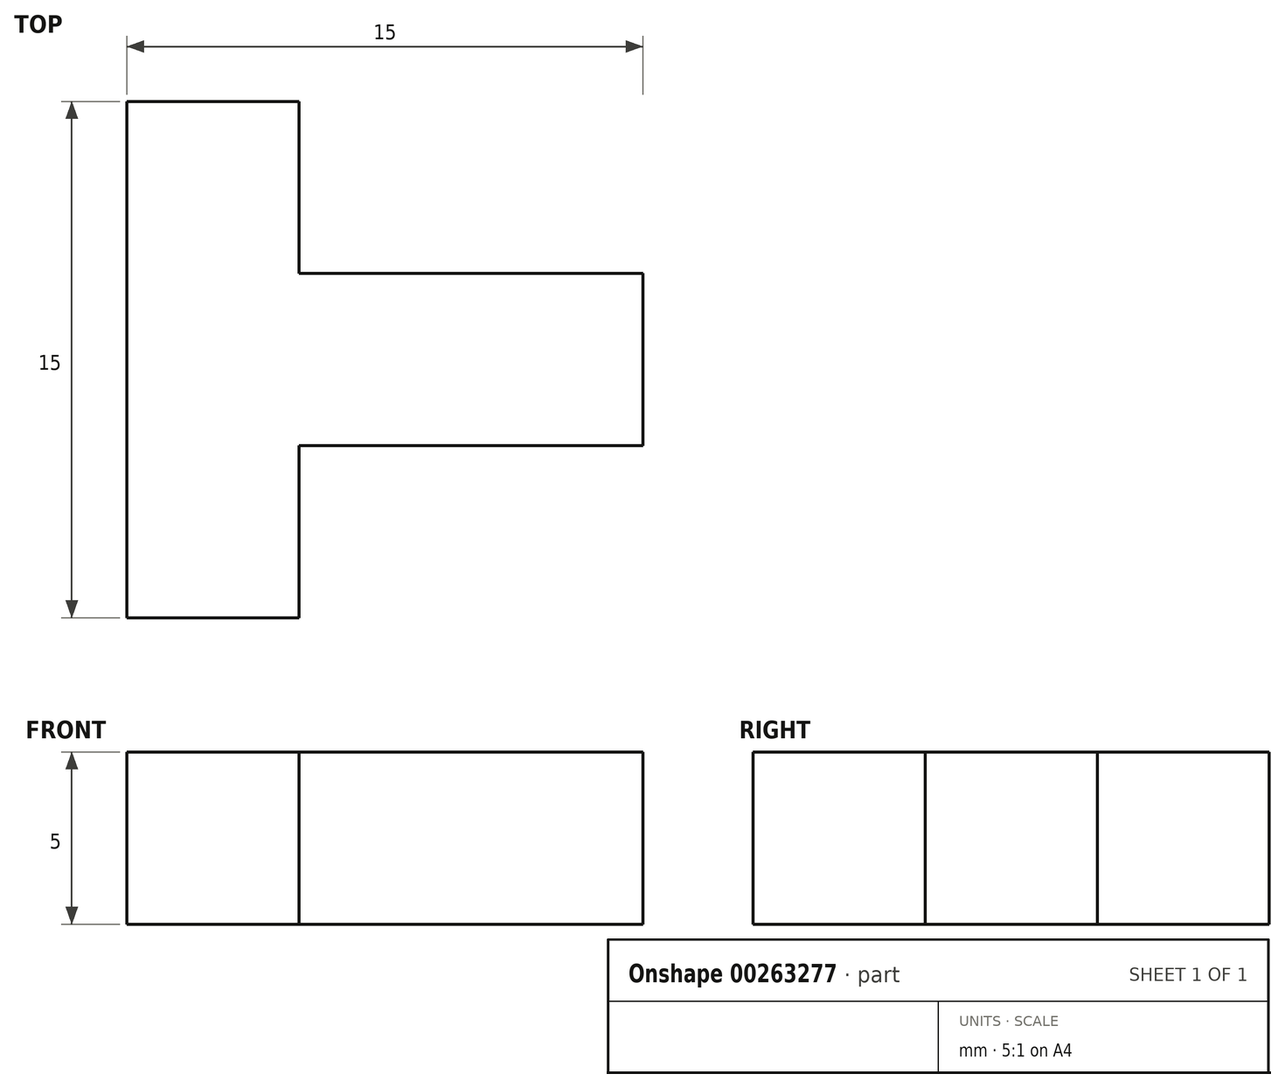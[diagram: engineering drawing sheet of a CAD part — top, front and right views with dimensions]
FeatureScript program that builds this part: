
annotation { "Feature Type Name" : "Feature", "Feature Type Description" : "" }
export const myFeature = defineFeature(function(context is Context, id is Id, definition is map)
    precondition{}
    {
        {
            var Q0;
            Q0=qCreatedBy(makeId("Top.planeOp"),FACE);
            var sketch = newSketch(context, id + "F0", { "sketchPlane" : qUnion([Q0])});
            skLineSegment(sketch, "E0.bottom", {"start": v(4.46, -2.5) * mm, "end": v(-5.54, -2.5) * mm});
            skLineSegment(sketch, "E0.top", {"start": v(4.46, 2.5) * mm, "end": v(-5.54, 2.5) * mm});
            skLineSegment(sketch, "E0.left", {"start": v(4.46, -2.5) * mm, "end": v(4.46, 2.5) * mm});
            skLineSegment(sketch, "E0.right", {"start": v(-5.54, -2.5) * mm, "end": v(-5.54, 2.5) * mm});
            skPoint(sketch, "E0.middle", {"position": v(-0.54, 0) * mm});
            skSolve(sketch);
        }
        {
            var Q0;
            Q0 = qSketchRegion(id + "F0", true);
            extrude(context, id + "F1", {"entities" : qUnion([Q0]), "depth" : 5 * mm});
        }
        {
            var Q0;
            Q0=makeQuery(id+"F1.opExtrude","CAP_FACE",FACE,{"disambiguationData":[OSD([sQuery(id+"F0.wireOp",EDGE,"E0.bottom"),sQuery(id+"F0.wireOp",EDGE,"E0.top"),sQuery(id+"F0.wireOp",EDGE,"E0.left"),sQuery(id+"F0.wireOp",EDGE,"E0.right")])],"isStart":false});
            var sketch = newSketch(context, id + "F2", { "sketchPlane" : qUnion([Q0])});
            skLineSegment(sketch, "E1.bottom", {"start": v(-5.54, 0) * mm, "end": v(-10.54, 0) * mm});
            skLineSegment(sketch, "E1.top", {"start": v(-5.54, -7.5) * mm, "end": v(-10.54, -7.5) * mm});
            skLineSegment(sketch, "E1.left", {"start": v(-5.54, 0) * mm, "end": v(-5.54, -7.5) * mm});
            skLineSegment(sketch, "E1.right", {"start": v(-10.54, 0) * mm, "end": v(-10.54, -7.5) * mm});
            skLineSegment(sketch, "E2.top", {"start": v(-5.54, 7.5) * mm, "end": v(-10.54, 7.5) * mm});
            skLineSegment(sketch, "E2.left", {"start": v(-5.54, 0) * mm, "end": v(-5.54, 7.5) * mm});
            skLineSegment(sketch, "E2.right", {"start": v(-10.54, 0) * mm, "end": v(-10.54, 7.5) * mm});
            skSolve(sketch);
        }
        {
            var Q0;
            Q0 = qSketchRegion(id + "F2", true);
            extrude(context, id + "F3", {"entities" : qUnion([Q0]), "operationType" : NewBodyOperationType.ADD, "oppositeDirection" : true, "depth" : 5 * mm});
        }
    });
